# Revit family: 0051210 Lighting Fixture_Sylvania_Rana LED 187x1183-Electronic-4000K_Surface Mounted
name_source: partatom
category: Lighting Fixtures
revit_build: Autodesk Revit 2015 (Build: 20140606_1530(x64)
units: mm (PartAtom-declared; Revit-internal decimal feet)

## types (2) — shared parameters
Accessory Material = Aluminum_Sylvania_RanaLED_White
Apparent Load = 32 VA
Assembly Code = D5020200
Color Filter = 16777215
Description = Provides perfect uniform light distribution greatly enhancing the lit space. Low profile for ease of installation in restricted ceiling voids. Two stage optic for optimum comfort and efficiency. UGR19 office compliant. Enclosed design reduces dust ingress and improves Lumen Maintenance Factor (LMF). 32W - 69W LED surface luminaire. Rana LED is perfect for office lighting applications, schools, airports and general lighting applications. Available with a satin optic and micro prism diffuser. Available in surface (615 X 615, 1183 X 1187). Rana LED delivers high efficiency up to 6,050lm (luminaire lumen output on 4,000K version), equating to 101lm/W (total system efficiency). Available in warm white (3,000K) and neutral white (4,000K). Integrated LED solution that has the same aesthetics as a T5 or T8 diffuse luminaire. Energy efficient electronic gear including DALI and 3 hour emergency versions as standard. Long lifetime: 50,000 hours life at 70% of the original output L70. Less maintenance is required due to the long lifetime of 50,000hrs. Energy Class: A++, A+, A. LED technology provides an energy efficient solution with reduced maintenance costs. Comes complete with safety cable
Dimming Lamp Color Temperature Shift = <None>
Emit Shape Visible in Rendering = No
Emit from Rectangle Length = 1153 mm
Emit from Rectangle Width = 65 mm  [stored 0.213255 ft]
Energy Class = A++, A+, A
Height = 47 mm  [stored 0.154199 ft]
IK Rating = 07
IP Rating = 20
Lamp = Integrated LED
Length = 1183 mm  [stored 3.88123 ft]
Life = 50 000h
Louver Length = 1153 mm
Manufacturer = Feilo Sylvania
Product Family = Rana LED 187x1183-Electronic-4000K Lamp
Product Page URL = http://www.feilosylvania.com
Reflector Material = Steel_Sylvania_RanaLED_Silver
Tilt Angle = -90.00°
URL = http://www.feilosylvania.com
Voltage = 230 V
Voltage Comments = UNV (Universal Voltage; 220-240 Volt)
Weight = 3.60 kg
Width = 187 mm  [stored 0.613517 ft]
zero-valued in all types: Default Elevation

## per-type parameters (varying)
| type | Catalog Number | Photometric Web File |
| RANA LED D W CM+P 1*LH 3K | 0051215 RANA LED D W CM+P 1*LH 3K | 0051215_RANALEDDWCM+P1LH3K-186482.ies |
| RANA LED D W CM+P 1*LH 4K | 0051210 RANA LED D W CM+P 1*LH 4K | 0051210_RANALEDDWCM+P1LH4K-186521.ies |

note: column(s) folded — value = type name in every type: Model

note: [stored X ft] marks values corroborated as IEEE doubles in the binary element streams (Revit-internal decimal feet)

## geometry (parser evidence)
native form markers: Blend x7, Sweep x5
no freeform markers — native parametric forms only
